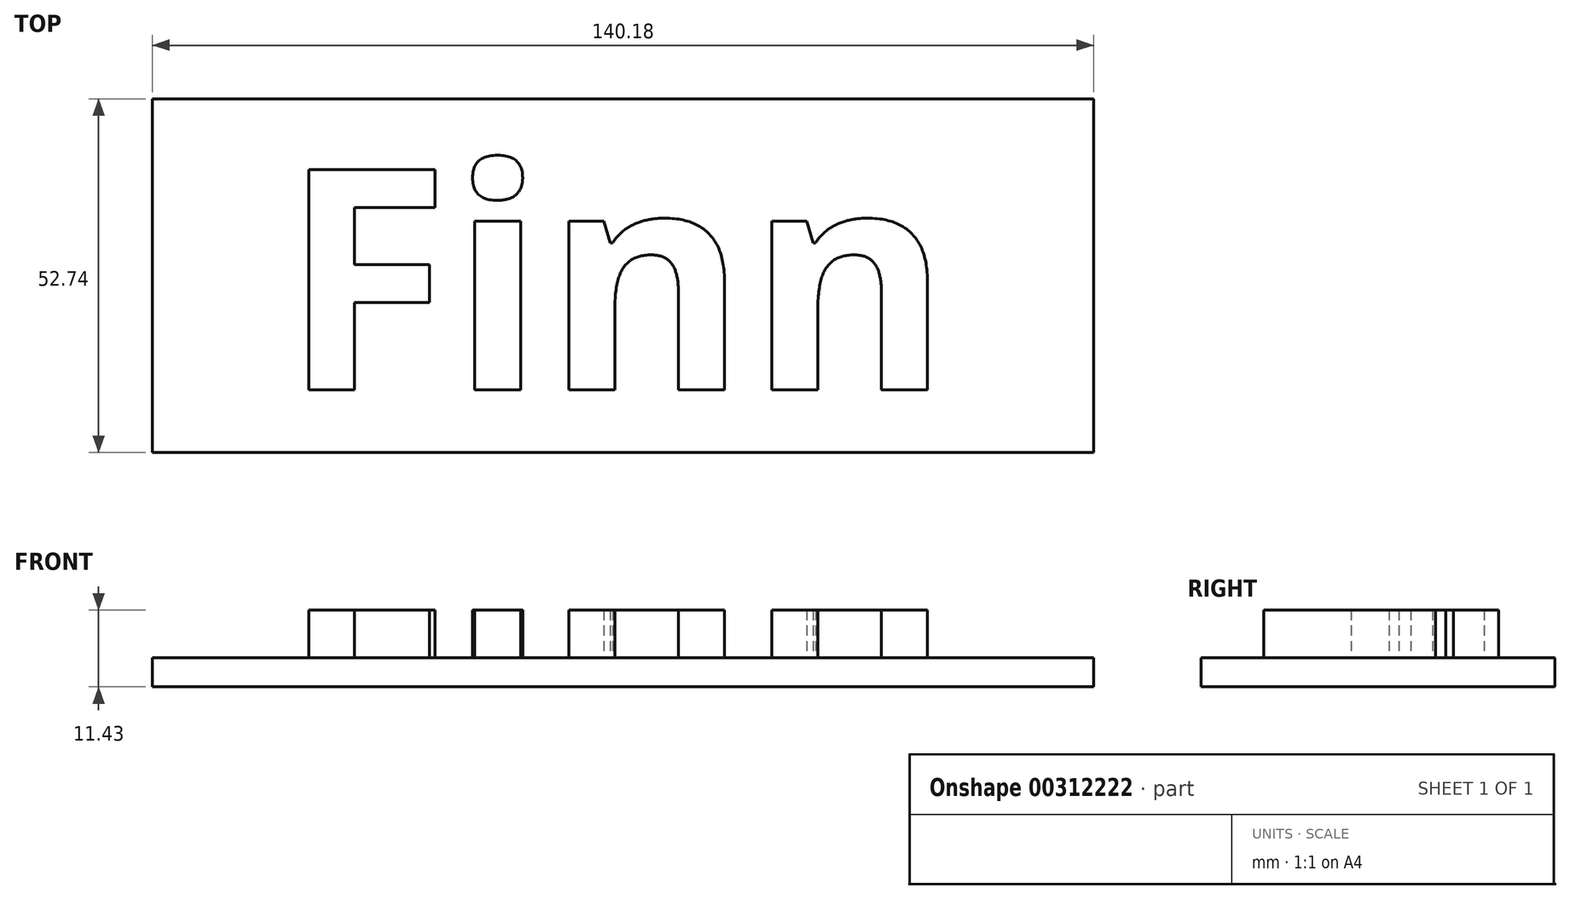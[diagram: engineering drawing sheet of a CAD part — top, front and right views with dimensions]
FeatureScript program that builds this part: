
annotation { "Feature Type Name" : "Feature", "Feature Type Description" : "" }
export const myFeature = defineFeature(function(context is Context, id is Id, definition is map)
    precondition{}
    {
        {
            var Q0;
            Q0=qCreatedBy(makeId("Top.planeOp"),FACE);
            var sketch = newSketch(context, id + "F0", { "sketchPlane" : qUnion([Q0])});
            skLineSegment(sketch, "E0.bottom", {"start": v(-66.83, 25.88) * mm, "end": v(73.35, 25.88) * mm});
            skLineSegment(sketch, "E0.top", {"start": v(-66.83, -26.86) * mm, "end": v(73.35, -26.86) * mm});
            skLineSegment(sketch, "E0.left", {"start": v(-66.83, 25.88) * mm, "end": v(-66.83, -26.86) * mm});
            skLineSegment(sketch, "E0.right", {"start": v(73.35, 25.88) * mm, "end": v(73.35, -26.86) * mm});
            skSolve(sketch);
        }
        {
            var Q0;
            Q0 = qSketchRegion(id + "F0", true);
            extrude(context, id + "F1", {"entities" : qUnion([Q0]), "depth" : 4.32 * mm});
        }
        {
            var Q0;
            Q0=makeQuery(id+"F1.opExtrude","CAP_FACE",FACE,{"disambiguationData":[OSD([sQuery(id+"F0.wireOp",EDGE,"E0.bottom"),sQuery(id+"F0.wireOp",EDGE,"E0.top"),sQuery(id+"F0.wireOp",EDGE,"E0.left"),sQuery(id+"F0.wireOp",EDGE,"E0.right")])],"isStart":false});
            var sketch = newSketch(context, id + "F2", { "sketchPlane" : qUnion([Q0])});
            skText(sketch, "E1", { "text": "Finn", "fontName": "OpenSans-Bold.ttf"});
            const initialGuessF2  = {"E1": [-0.0477, -0.0175, 1, 0, 0.03312]};
            skSetInitialGuess(sketch, initialGuessF2);
            skSolve(sketch);
        }
        {
            var Q0;
            Q0 = qSketchRegion(id + "F2", true);
            extrude(context, id + "F3", {"entities" : qUnion([Q0]), "operationType" : NewBodyOperationType.ADD, "depth" : 7.11 * mm});
        }
    });
